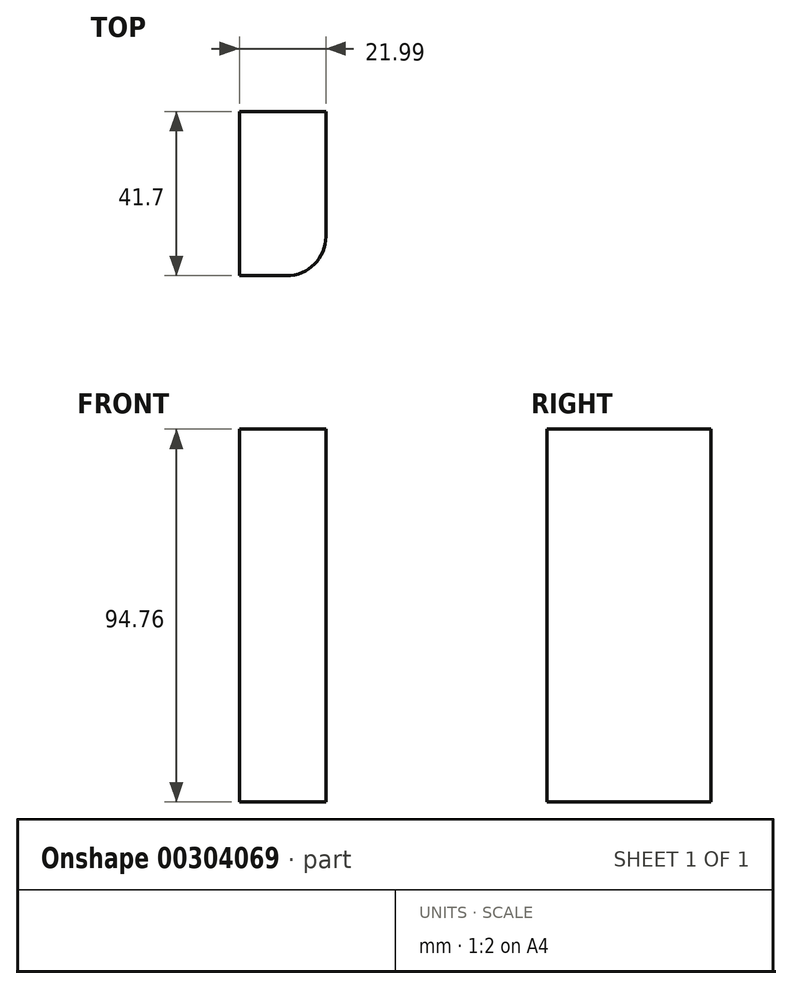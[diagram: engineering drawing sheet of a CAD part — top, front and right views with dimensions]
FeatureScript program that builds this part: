
annotation { "Feature Type Name" : "Feature", "Feature Type Description" : "" }
export const myFeature = defineFeature(function(context is Context, id is Id, definition is map)
    precondition{}
    {
        {
            var Q0;
            Q0=qCreatedBy(makeId("Top.planeOp"),FACE);
            var sketch = newSketch(context, id + "F0", { "sketchPlane" : qUnion([Q0])});
            skLineSegment(sketch, "E0.bottom", {"start": v(-35.27, -18.46) * mm, "end": v(-13.28, -18.46) * mm});
            skLineSegment(sketch, "E0.top", {"start": v(-35.27, 23.24) * mm, "end": v(-13.28, 23.24) * mm});
            skLineSegment(sketch, "E0.left", {"start": v(-35.27, -18.46) * mm, "end": v(-35.27, 23.24) * mm});
            skLineSegment(sketch, "E0.right", {"start": v(-13.28, -18.46) * mm, "end": v(-13.28, 23.24) * mm});
            skSolve(sketch);
        }
        {
            var Q0;
            Q0=makeQuery(id+"F0.imprint","IMPRINT",FACE,{"disambiguationData":[TD([[makeQuery(id+"F0.imprint","IMPRINT",EDGE,{"derivedFrom":sQuery(id+"F0.wireOp",EDGE,"E0.bottom")}),1.0]])]});
            extrude(context, id + "F1", {"entities" : qUnion([Q0]), "depth" : 94.76 * mm});
        }
        {
            var Q0;
            Q0=makeQuery(id+"F1.opExtrude","SWEPT_EDGE",EDGE,{"disambiguationData":[OSD([sQuery(id+"F0.wireOp",EDGE,"E0.bottom"),sQuery(id+"F0.wireOp",EDGE,"E0.right")])]});
            fillet(context, id + "F2", {"entities" : qUnion([Q0]), "radius" : 9.94 * mm, "tangentPropagation" : true, "allowEdgeOverflow" : false});
        }
    });
